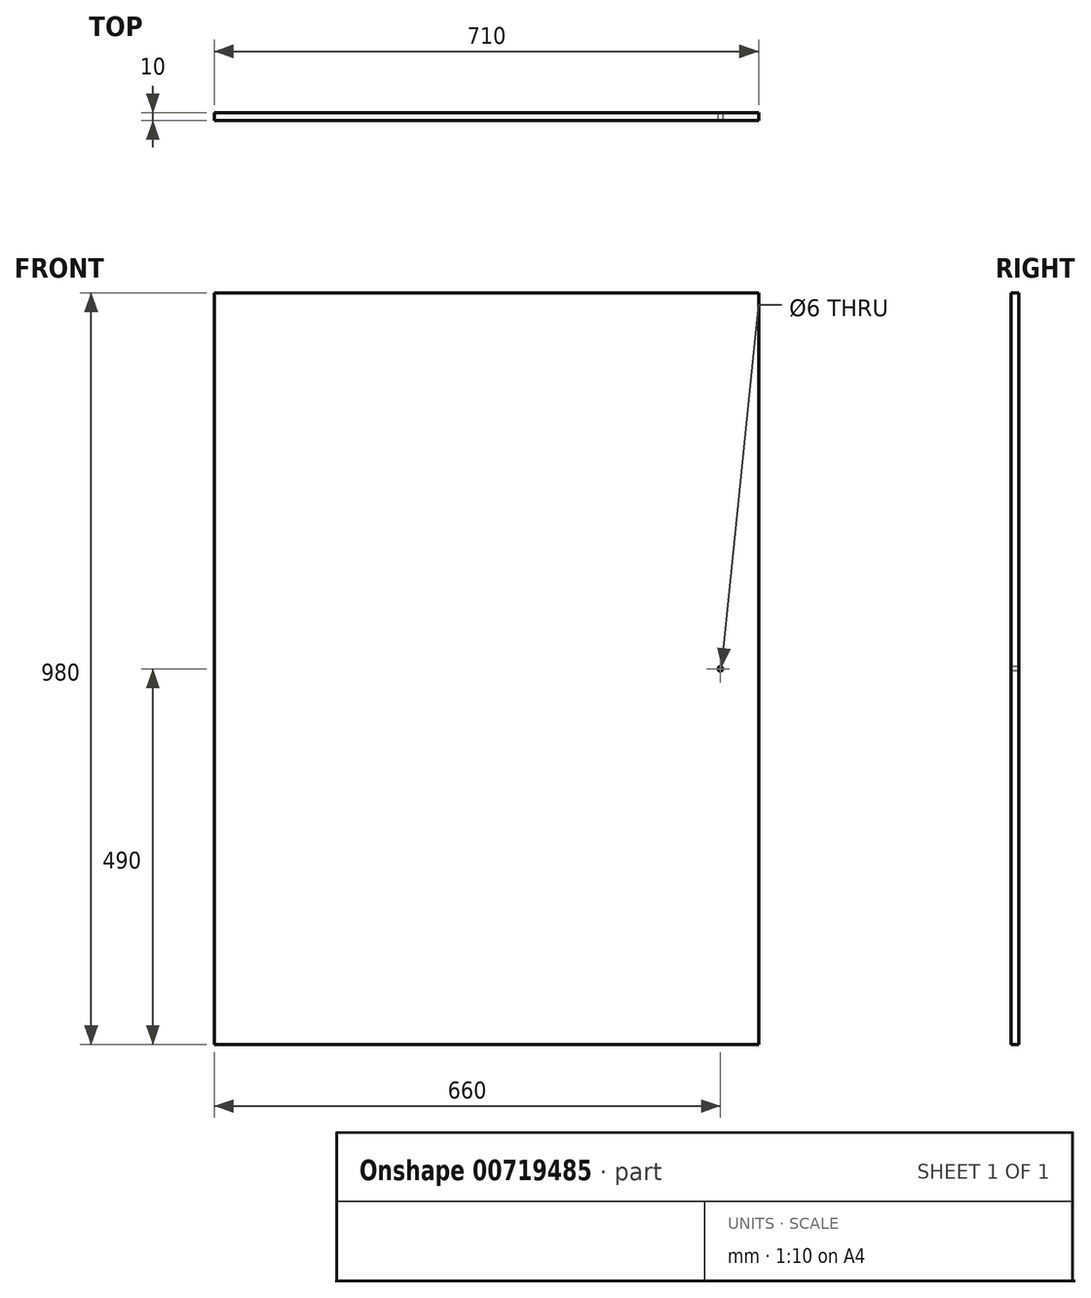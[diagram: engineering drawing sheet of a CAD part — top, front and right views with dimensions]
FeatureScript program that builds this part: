
annotation { "Feature Type Name" : "Feature", "Feature Type Description" : "" }
export const myFeature = defineFeature(function(context is Context, id is Id, definition is map)
    precondition{}
    {
        {
            var Q0;
            Q0=qCreatedBy(makeId("Front.planeOp"),FACE);
            var sketch = newSketch(context, id + "F0", { "sketchPlane" : qUnion([Q0])});
            skLineSegment(sketch, "E0.bottom", {"start": v(0, 0) * mm, "end": v(710, 0) * mm});
            skLineSegment(sketch, "E0.top", {"start": v(0, 980) * mm, "end": v(710, 980) * mm});
            skLineSegment(sketch, "E0.left", {"start": v(0, 0) * mm, "end": v(0, 980) * mm});
            skLineSegment(sketch, "E0.right", {"start": v(710, 0) * mm, "end": v(710, 980) * mm});
            skSolve(sketch);
        }
        {
            var Q0;
            Q0=makeQuery(id+"F0.imprint","IMPRINT",FACE,{"disambiguationData":[TD([[makeQuery(id+"F0.imprint","IMPRINT",EDGE,{"derivedFrom":sQuery(id+"F0.wireOp",EDGE,"E0.bottom")}),1.0]])]});
            extrude(context, id + "F1", {"entities" : qUnion([Q0]), "depth" : 10 * mm, "offsetDistance" : 25 * mm});
        }
        {
            var Q0;
            Q0=makeQuery(id+"F1.opExtrude","CAP_FACE",FACE,{"disambiguationData":[OSD([sQuery(id+"F0.wireOp",EDGE,"E0.bottom"),sQuery(id+"F0.wireOp",EDGE,"E0.top"),sQuery(id+"F0.wireOp",EDGE,"E0.left"),sQuery(id+"F0.wireOp",EDGE,"E0.right")])],"isStart":false});
            var sketch = newSketch(context, id + "F2", { "sketchPlane" : qUnion([Q0])});
            skLineSegment(sketch, "E1", {"start": v(660, 980) * mm, "end": v(660, 0) * mm, "construction": true});
            skCircle(sketch, "E2", {"center": v(660, 490) * mm, "radius": 3 * mm});
            skSolve(sketch);
        }
        {
            var Q0;
            Q0 = qSketchRegion(id + "F2", true);
            extrude(context, id + "F3", {"entities" : qUnion([Q0]), "operationType" : NewBodyOperationType.REMOVE, "endBound" : BoundingType.THROUGH_ALL, "oppositeDirection" : true, "depth" : 25 * mm, "offsetDistance" : 25 * mm});
        }
    });
